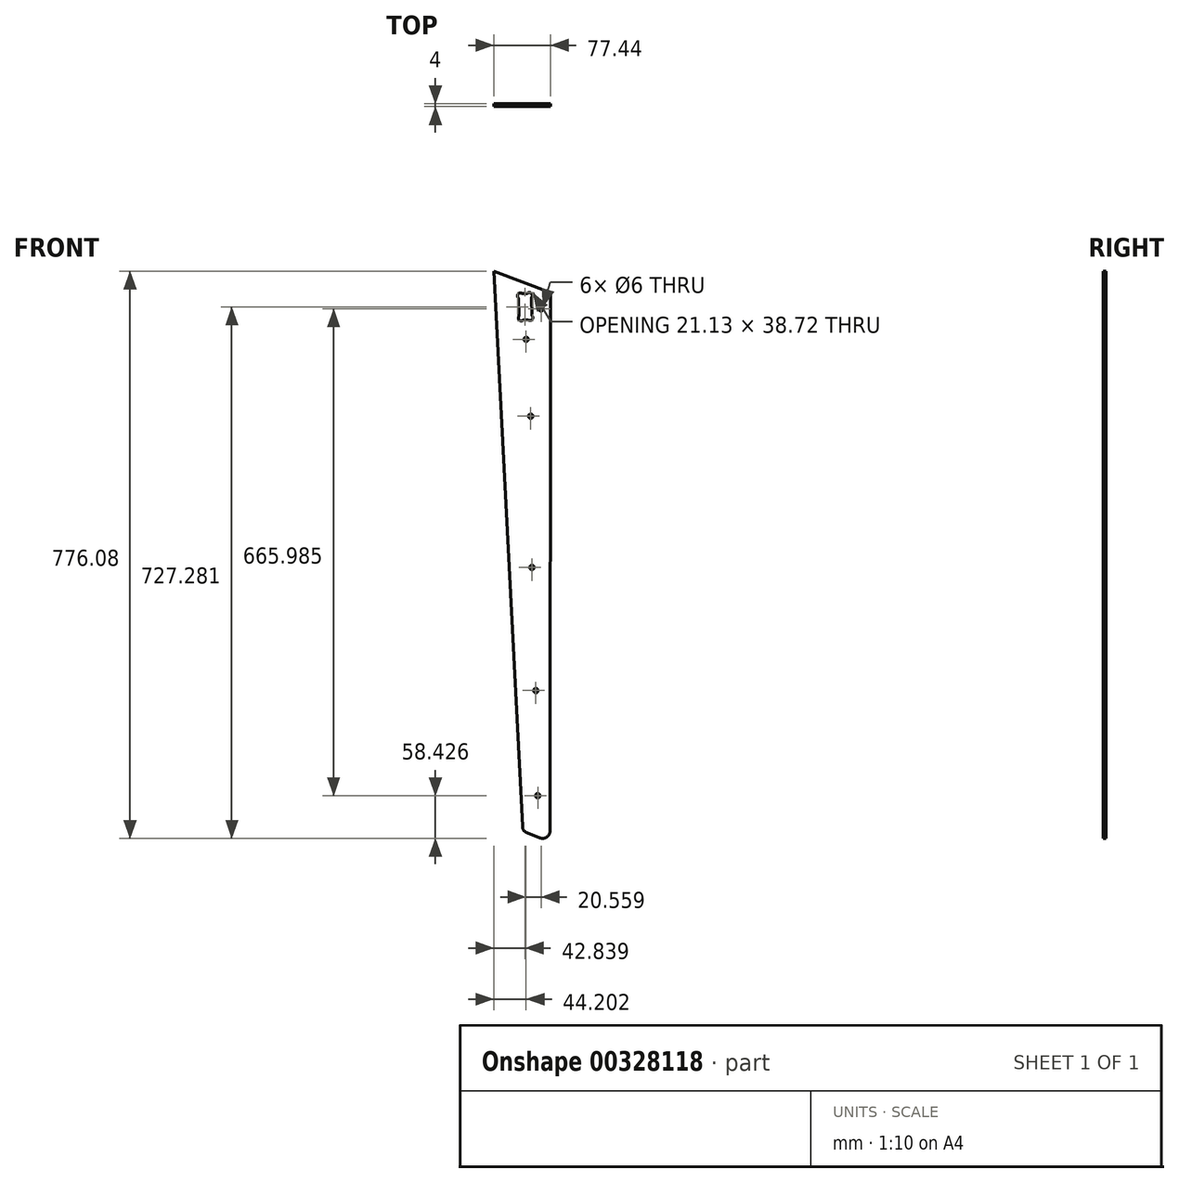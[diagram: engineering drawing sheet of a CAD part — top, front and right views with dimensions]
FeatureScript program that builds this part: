
annotation { "Feature Type Name" : "Feature", "Feature Type Description" : "" }
export const myFeature = defineFeature(function(context is Context, id is Id, definition is map)
    precondition{}
    {
        {
            var Q0;
            Q0=qCreatedBy(makeId("Front.planeOp"),FACE);
            var sketch = newSketch(context, id + "F0", { "sketchPlane" : qUnion([Q0])});
            skLineSegment(sketch, "E0", {"start": v(-41.3, 458.1) * mm, "end": v(-47.58, 457.9) * mm});
            skArc(sketch, "E1", {"start": v(-47.58, 457.9) * mm, "mid": v(-53.25, 457.74) * mm, "end": v(-53.38, 463.41) * mm});
            skLineSegment(sketch, "E2", {"start": v(-53.38, 463.41) * mm, "end": v(-54.4, 488) * mm});
            skArc(sketch, "E3", {"start": v(-54.4, 488) * mm, "mid": v(-54.64, 493.67) * mm, "end": v(-48.96, 493.87) * mm});
            skLineSegment(sketch, "E4", {"start": v(-48.96, 493.87) * mm, "end": v(-42.28, 494.1) * mm});
            skArc(sketch, "E5", {"start": v(-42.28, 494.1) * mm, "mid": v(-36.6, 494.26) * mm, "end": v(-36.49, 488.58) * mm});
            skLineSegment(sketch, "E6", {"start": v(-36.49, 488.58) * mm, "end": v(-35.87, 463.99) * mm});
            skArc(sketch, "E7", {"start": v(-35.87, 463.99) * mm, "mid": v(-35.62, 458.31) * mm, "end": v(-41.3, 458.1) * mm});
            skLineSegment(sketch, "E8", {"start": v(-24.74, -250.62) * mm, "end": v(-42.39, -243.89) * mm});
            skArc(sketch, "E9", {"start": v(-42.39, -243.89) * mm, "mid": v(-46.91, -240.43) * mm, "end": v(-48.81, -235.06) * mm});
            skLineSegment(sketch, "E10", {"start": v(-48.81, -235.06) * mm, "end": v(-87.97, 524.8) * mm});
            skLineSegment(sketch, "E11", {"start": v(-87.97, 524.8) * mm, "end": v(-10.53, 495.27) * mm});
            skLineSegment(sketch, "E12", {"start": v(-10.53, 495.27) * mm, "end": v(-11.17, -241.29) * mm});
            skArc(sketch, "E13", {"start": v(-11.17, -241.29) * mm, "mid": v(-15.5, -249.51) * mm, "end": v(-24.74, -250.62) * mm});
            skCircle(sketch, "E14", {"center": v(-37.61, 326.29) * mm, "radius": 3 * mm});
            skCircle(sketch, "E15", {"center": v(-35.82, 119.28) * mm, "radius": 3 * mm});
            skCircle(sketch, "E16", {"center": v(-23.2, 473.13) * mm, "radius": 3 * mm});
            skCircle(sketch, "E17", {"center": v(-30.54, -49.06) * mm, "radius": 3 * mm});
            skCircle(sketch, "E18", {"center": v(-27.88, -192.85) * mm, "radius": 3 * mm});
            skCircle(sketch, "E19", {"center": v(-43.77, 431.4) * mm, "radius": 3 * mm});
            skSolve(sketch);
        }
        {
            var Q0;
            Q0=makeQuery(id+"F0.imprint","IMPRINT",FACE,{"disambiguationData":[TD([[makeQuery(id+"F0.imprint","IMPRINT",EDGE,{"derivedFrom":sQuery(id+"F0.wireOp",EDGE,"E19")}),-1.0]])]});
            var Q1;
            Q1=makeQuery(id+"F0.imprint","IMPRINT",FACE,{"disambiguationData":[TD([[makeQuery(id+"F0.imprint","IMPRINT",EDGE,{"derivedFrom":sQuery(id+"F0.wireOp",EDGE,"E16")}),-1.0]])]});
            var Q2;
            Q2=makeQuery(id+"F0.imprint","IMPRINT",FACE,{"disambiguationData":[TD([[makeQuery(id+"F0.imprint","IMPRINT",EDGE,{"derivedFrom":sQuery(id+"F0.wireOp",EDGE,"E14")}),-1.0]])]});
            var Q3;
            Q3=makeQuery(id+"F0.imprint","IMPRINT",FACE,{"disambiguationData":[TD([[makeQuery(id+"F0.imprint","IMPRINT",EDGE,{"derivedFrom":sQuery(id+"F0.wireOp",EDGE,"E15")}),-1.0]])]});
            var Q4;
            Q4=makeQuery(id+"F0.imprint","IMPRINT",FACE,{"disambiguationData":[TD([[makeQuery(id+"F0.imprint","IMPRINT",EDGE,{"derivedFrom":sQuery(id+"F0.wireOp",EDGE,"E18")}),-1.0]])]});
            var Q5;
            Q5=makeQuery(id+"F0.imprint","IMPRINT",FACE,{"disambiguationData":[TD([[makeQuery(id+"F0.imprint","IMPRINT",EDGE,{"derivedFrom":sQuery(id+"F0.wireOp",EDGE,"E0")}),1.0]])]});
            var Q6;
            Q6=makeQuery(id+"F0.imprint","IMPRINT",FACE,{"disambiguationData":[TD([[makeQuery(id+"F0.imprint","IMPRINT",EDGE,{"derivedFrom":sQuery(id+"F0.wireOp",EDGE,"E17")}),-1.0]])]});
            extrude(context, id + "F1", {"entities" : qUnion([Q0, Q1, Q2, Q3, Q4, Q5, Q6]), "oppositeDirection" : true, "depth" : 18 * mm});
        }
        {
            var Q0;
            Q0=makeQuery(id+"F0.imprint","IMPRINT",FACE,{"disambiguationData":[TD([[makeQuery(id+"F0.imprint","IMPRINT",EDGE,{"derivedFrom":sQuery(id+"F0.wireOp",EDGE,"E19")}),-1.0]])]});
            var Q1;
            Q1=makeQuery(id+"F0.imprint","IMPRINT",FACE,{"disambiguationData":[TD([[makeQuery(id+"F0.imprint","IMPRINT",EDGE,{"derivedFrom":sQuery(id+"F0.wireOp",EDGE,"E16")}),-1.0]])]});
            var Q2;
            Q2=makeQuery(id+"F0.imprint","IMPRINT",FACE,{"disambiguationData":[TD([[makeQuery(id+"F0.imprint","IMPRINT",EDGE,{"derivedFrom":sQuery(id+"F0.wireOp",EDGE,"E14")}),-1.0]])]});
            var Q3;
            Q3=makeQuery(id+"F0.imprint","IMPRINT",FACE,{"disambiguationData":[TD([[makeQuery(id+"F0.imprint","IMPRINT",EDGE,{"derivedFrom":sQuery(id+"F0.wireOp",EDGE,"E15")}),-1.0]])]});
            var Q4;
            Q4=makeQuery(id+"F0.imprint","IMPRINT",FACE,{"disambiguationData":[TD([[makeQuery(id+"F0.imprint","IMPRINT",EDGE,{"derivedFrom":sQuery(id+"F0.wireOp",EDGE,"E18")}),-1.0]])]});
            var Q5;
            Q5=makeQuery(id+"F0.imprint","IMPRINT",FACE,{"disambiguationData":[TD([[makeQuery(id+"F0.imprint","IMPRINT",EDGE,{"derivedFrom":sQuery(id+"F0.wireOp",EDGE,"E17")}),-1.0]])]});
            extrude(context, id + "F2", {"entities" : qUnion([Q0, Q1, Q2, Q3, Q4, Q5]), "operationType" : NewBodyOperationType.REMOVE, "oppositeDirection" : true, "depth" : 14 * mm});
        }
    });
